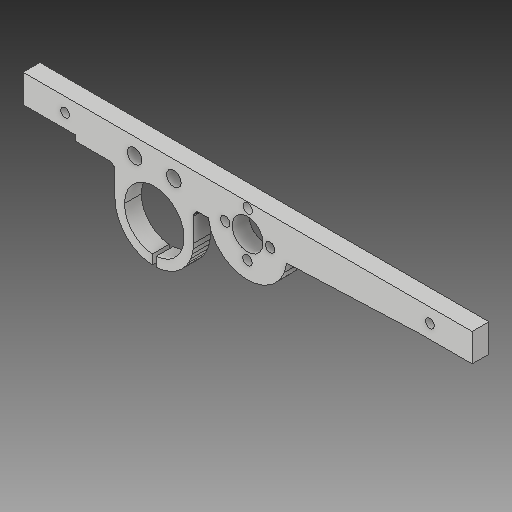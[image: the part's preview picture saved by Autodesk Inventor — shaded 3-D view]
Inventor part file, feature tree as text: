
AUTODESK INVENTOR PART (.ipt)
format: ipt  version: 2017 (Build 210142000, 142)  size: 408,576 bytes
history: native  units: mm
features: sketch x8, reference x5, extrude x4, hole x4, other x4
ambient origin geometry x8: Origin, YZ Plane, XZ Plane, XY Plane, X Axis, Y Axis, Z Axis, Center Point
bodies: Solid1 (feature_tree)
feature tree (25):
  extrude  "Extrusion1"  Depth=6.0mm
  extrude  "Extrusion2"  Depth=6.0mm TaperAngle=0.0deg
  hole  "Hole1"  [1 undecoded]
  hole  "Hole2"  [1 undecoded]
  hole  "Hole3"  [1 undecoded]
  hole  "Hole4"  [1 undecoded]
  extrude  "Extrusion3"  [1 undecoded]
  extrude  "Extrusion4"  [1 undecoded]
  sketch  "Sketch1"  dims[d0=6.0mm d1=0.0mm d2=3.2mm]
  sketch  "Sketch2"  dims[d3=6.0mm d4=0.0mm]
  sketch  "Sketch3"  dims[d5=3.2mm d6=6.0mm d7=4.0mm d8=2.0mm d9=90.0deg d10=8.0mm d11=20.594885mm]
  sketch  "Sketch4"  dims[d12=21.2mm d13=6.0mm d14=4.0mm d15=2.0mm d16=90.0deg d17=8.0mm d18=20.594885mm]
  sketch  "Sketch5"  dims[d19=21.2mm d20=6.0mm d21=4.0mm d22=2.0mm d23=90.0deg d24=8.0mm d25=20.594885mm]
  reference  "Reference1"
  sketch  "Sketch6"  dims[d26=3.2mm d27=6.0mm d28=4.0mm d29=2.0mm d30=90.0deg d31=8.0mm d32=20.594885mm d33=6.0mm d34=0.0mm]
  sketch  "Sketch7"  dims[d35=6.0mm d36=0.0mm]
  sketch  "Sketch8"
  reference  "Reference2"
  reference  "Reference3"
  reference  "Reference4"
  reference  "Reference5"
  other  "<userpath>\OneDrive\Inventor\Beast 3D Printer\Rear-Bed-Holder.iam"
  other  "Rear-Bed-Holder.iam"
  other  "Left Bed Holder Upper:1"
  other  "Brass-Nut:1"
note: 6 required parameter values undecoded (feature->parameter linkage not recoverable at this tier; creation-order binding heuristic only, values carry confidence <= 0.55)
